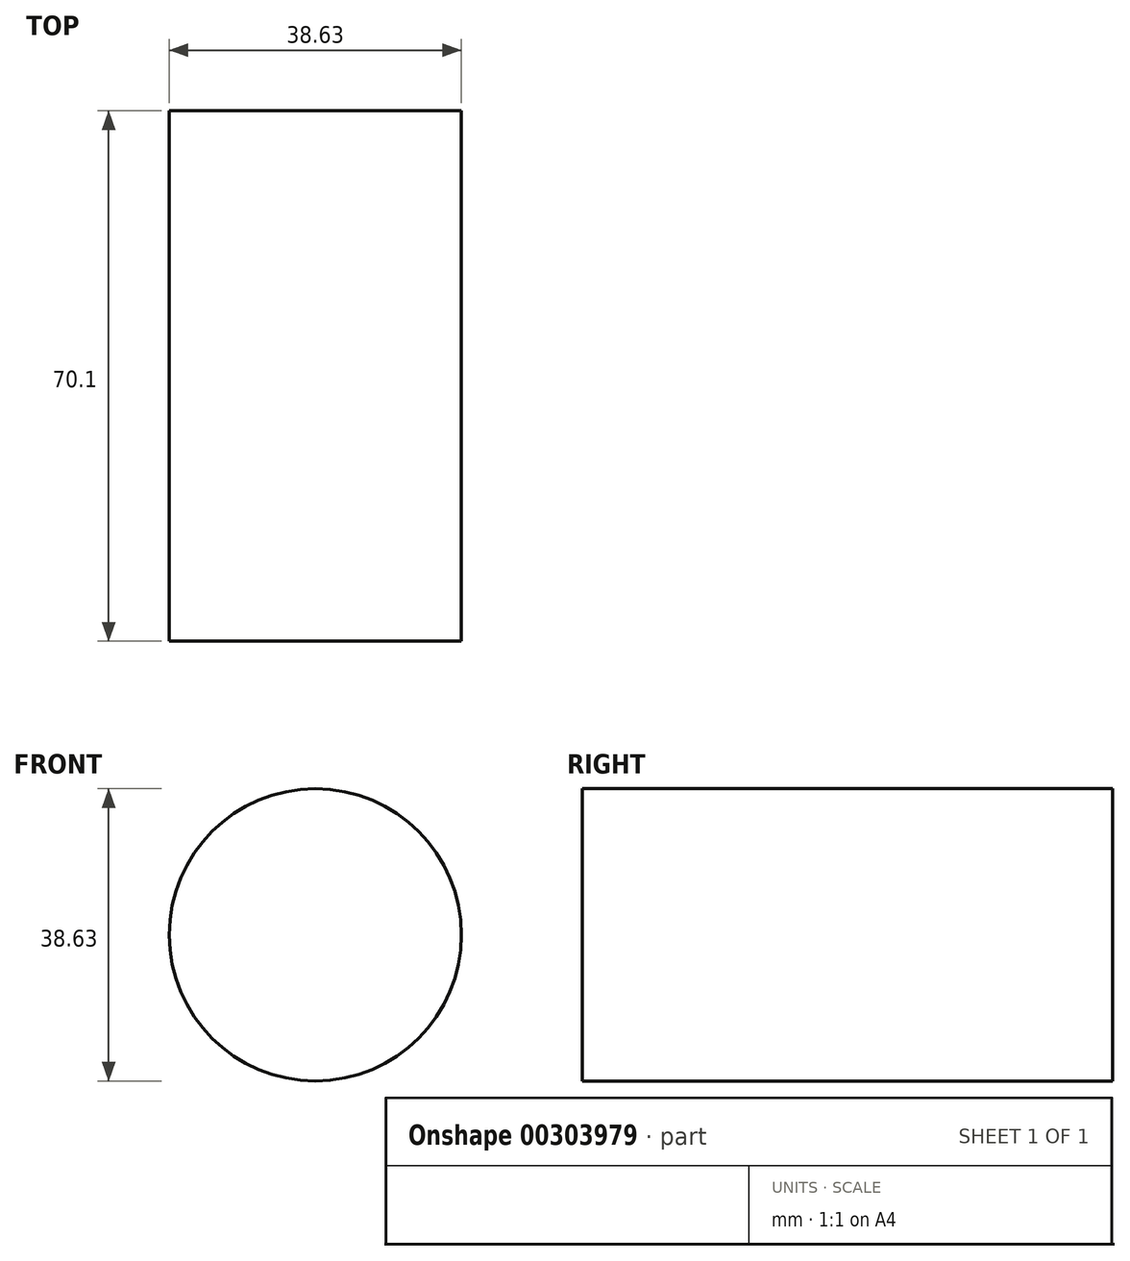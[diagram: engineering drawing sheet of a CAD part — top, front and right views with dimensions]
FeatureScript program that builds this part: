
annotation { "Feature Type Name" : "Feature", "Feature Type Description" : "" }
export const myFeature = defineFeature(function(context is Context, id is Id, definition is map)
    precondition{}
    {
        {
            var Q0;
            Q0=qCreatedBy(makeId("Front.planeOp"),FACE);
            var sketch = newSketch(context, id + "F0", { "sketchPlane" : qUnion([Q0])});
            skCircle(sketch, "E0", {"center": v(-24.5, 7.83) * mm, "radius": 19.31 * mm});
            skSolve(sketch);
        }
        {
            var Q0;
            Q0=makeQuery(id+"F0.imprint","IMPRINT",FACE,{"disambiguationData":[TD([[makeQuery(id+"F0.imprint","IMPRINT",EDGE,{"derivedFrom":sQuery(id+"F0.wireOp",EDGE,"E0")}),1.0]])]});
            extrude(context, id + "F1", {"entities" : qUnion([Q0]), "depth" : 70.1 * mm});
        }
    });
